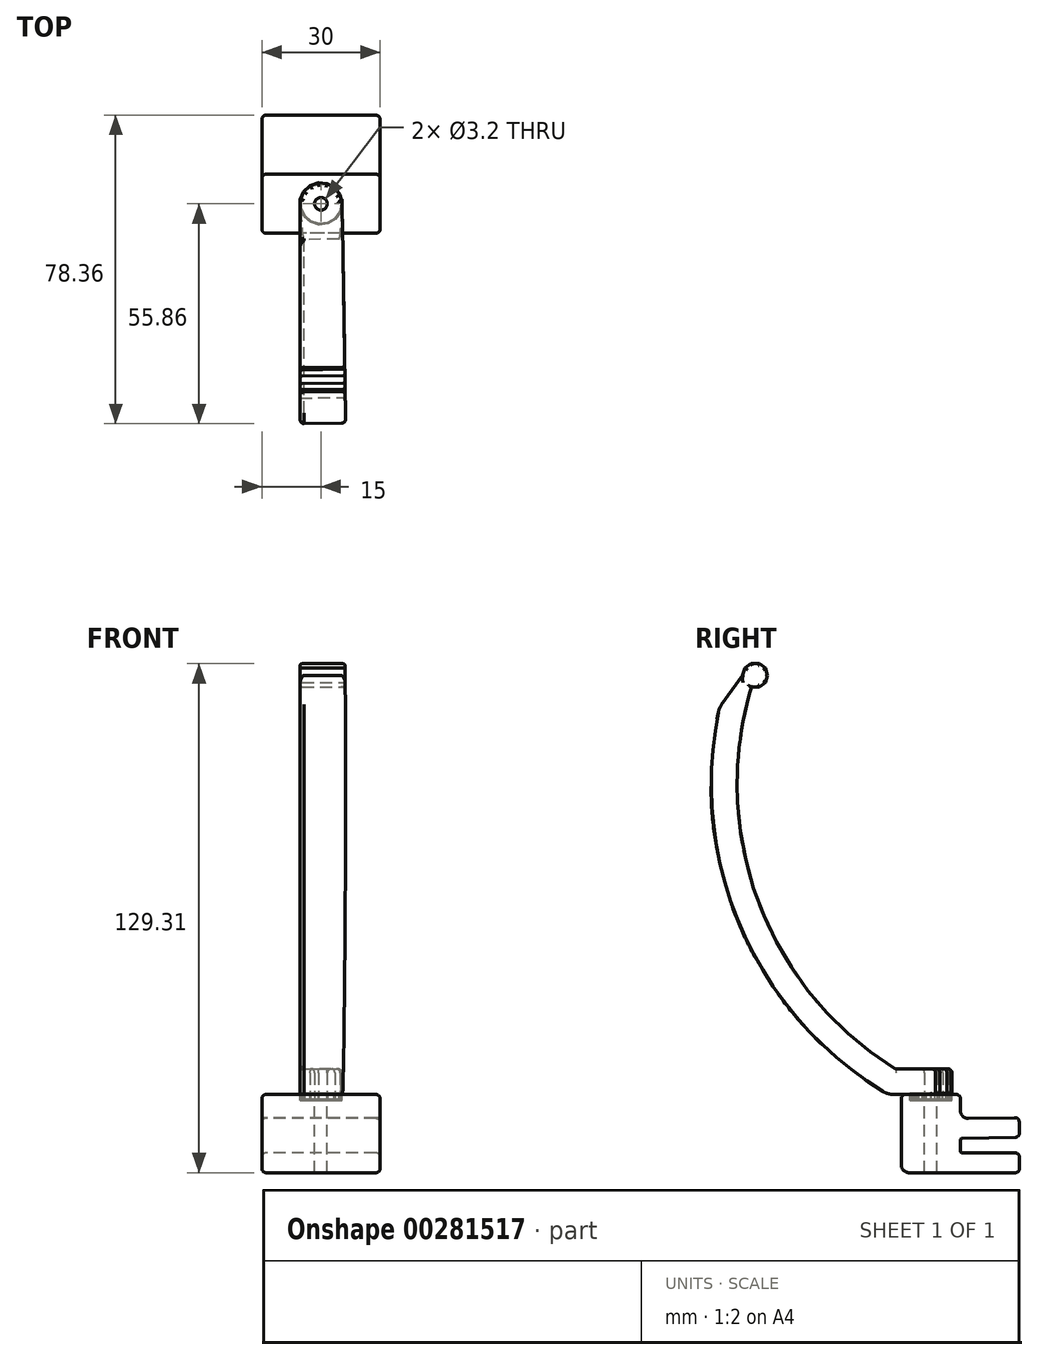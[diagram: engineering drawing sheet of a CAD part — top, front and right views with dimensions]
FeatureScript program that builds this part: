
annotation { "Feature Type Name" : "Feature", "Feature Type Description" : "" }
export const myFeature = defineFeature(function(context is Context, id is Id, definition is map)
    precondition{}
    {
        {
            var Q0;
            Q0=qCreatedBy(makeId("Right.planeOp"),FACE);
            var sketch = newSketch(context, id + "F0", { "sketchPlane" : qUnion([Q0])});
            skLineSegment(sketch, "E0", {"start": v(-1, 0) * mm, "end": v(-15, 0) * mm});
            skLineSegment(sketch, "E1", {"start": v(-14.5, 5) * mm, "end": v(-1, 5) * mm});
            skLineSegment(sketch, "E2", {"start": v(0, 4) * mm, "end": v(0, 1) * mm});
            skLineSegment(sketch, "E3", {"start": v(-15, 5.5) * mm, "end": v(-15, 8.26) * mm});
            skLineSegment(sketch, "E4", {"start": v(-1, 8.98) * mm, "end": v(-14.5, 8.76) * mm});
            skLineSegment(sketch, "E5", {"start": v(-0.02, 10) * mm, "end": v(-0.07, 13) * mm});
            skLineSegment(sketch, "E6", {"start": v(-1.08, 13.98) * mm, "end": v(-12.97, 13.78) * mm});
            skLineSegment(sketch, "E7", {"start": v(-15, 0) * mm, "end": v(-28, 0) * mm});
            skLineSegment(sketch, "E8", {"start": v(-30, 2) * mm, "end": v(-30, 12.86) * mm});
            skLineSegment(sketch, "E9", {"start": v(-15, 15.78) * mm, "end": v(-15, 18.86) * mm});
            skPoint(sketch, "E10.visualSharp", {"position": v(-15, 8.75) * mm});
            skArc(sketch, "E10.filletArc", {"start": v(-14.5, 8.76) * mm, "mid": v(-14.86, 8.6) * mm, "end": v(-15, 8.26) * mm});
            skPoint(sketch, "E11.visualSharp", {"position": v(-15, 5) * mm});
            skArc(sketch, "E11.filletArc", {"start": v(-15, 5.5) * mm, "mid": v(-14.85, 5.15) * mm, "end": v(-14.5, 5) * mm});
            skPoint(sketch, "E12.visualSharp", {"position": v(0, 5) * mm});
            skArc(sketch, "E12.filletArc", {"start": v(0, 4) * mm, "mid": v(-0.3, 4.7) * mm, "end": v(-1, 5) * mm});
            skPoint(sketch, "E13.visualSharp", {"position": v(0, 9) * mm});
            skArc(sketch, "E13.filletArc", {"start": v(-1, 8.98) * mm, "mid": v(-0.3, 9.29) * mm, "end": v(-0.02, 10) * mm});
            skPoint(sketch, "E14.visualSharp", {"position": v(-0.08, 14) * mm});
            skArc(sketch, "E14.filletArc", {"start": v(-0.07, 13) * mm, "mid": v(-0.37, 13.7) * mm, "end": v(-1.08, 13.98) * mm});
            skPoint(sketch, "E15.visualSharp", {"position": v(0, 0) * mm});
            skArc(sketch, "E15.filletArc", {"start": v(-1, 0) * mm, "mid": v(-0.3, 0.3) * mm, "end": v(0, 1) * mm});
            skPoint(sketch, "E16.visualSharp", {"position": v(-30, 0) * mm});
            skArc(sketch, "E16.filletArc", {"start": v(-30, 2) * mm, "mid": v(-29.41, 0.59) * mm, "end": v(-28, 0) * mm});
            skPoint(sketch, "E17.visualSharp", {"position": v(-15, 13.75) * mm});
            skArc(sketch, "E17.filletArc", {"start": v(-15, 15.78) * mm, "mid": v(-14.4, 14.36) * mm, "end": v(-12.97, 13.78) * mm});
            skLineSegment(sketch, "E18", {"start": v(-30, 12.86) * mm, "end": v(-30, 18.86) * mm});
            skLineSegment(sketch, "E19", {"start": v(-29, 19.86) * mm, "end": v(-16, 19.86) * mm});
            skPoint(sketch, "E20.orphan", {"position": v(-15, 12.86) * mm});
            skPoint(sketch, "E21.visualSharp", {"position": v(-15, 19.86) * mm});
            skArc(sketch, "E21.filletArc", {"start": v(-15, 18.86) * mm, "mid": v(-15.3, 19.57) * mm, "end": v(-16, 19.86) * mm});
            skPoint(sketch, "E22.visualSharp", {"position": v(-30, 19.86) * mm});
            skArc(sketch, "E22.filletArc", {"start": v(-29, 19.86) * mm, "mid": v(-29.7, 19.57) * mm, "end": v(-30, 18.86) * mm});
            skSolve(sketch);
        }
        {
            var Q0;
            Q0=makeQuery(id+"F0.imprint","IMPRINT",FACE,{"disambiguationData":[TD([[makeQuery(id+"F0.imprint","IMPRINT",EDGE,{"derivedFrom":sQuery(id+"F0.wireOp",EDGE,"E0")}),-1.0]])]});
            extrude(context, id + "F1", {"entities" : qUnion([Q0]), "endBound" : BoundingType.SYMMETRIC, "depth" : 30 * mm});
        }
        {
            var Q0;
            Q0=makeQuery(id+"F1.opExtrude","CAP_FACE",FACE,{"disambiguationData":[OSD([sQuery(id+"F0.wireOp",EDGE,"E0"),sQuery(id+"F0.wireOp",EDGE,"E1"),sQuery(id+"F0.wireOp",EDGE,"E2"),sQuery(id+"F0.wireOp",EDGE,"E3"),sQuery(id+"F0.wireOp",EDGE,"E4"),sQuery(id+"F0.wireOp",EDGE,"E5"),sQuery(id+"F0.wireOp",EDGE,"E6"),sQuery(id+"F0.wireOp",EDGE,"E7"),sQuery(id+"F0.wireOp",EDGE,"E8"),sQuery(id+"F0.wireOp",EDGE,"E9"),sQuery(id+"F0.wireOp",EDGE,"E10.filletArc"),sQuery(id+"F0.wireOp",EDGE,"E11.filletArc"),sQuery(id+"F0.wireOp",EDGE,"E12.filletArc"),sQuery(id+"F0.wireOp",EDGE,"E13.filletArc"),sQuery(id+"F0.wireOp",EDGE,"E14.filletArc"),sQuery(id+"F0.wireOp",EDGE,"E15.filletArc"),sQuery(id+"F0.wireOp",EDGE,"E16.filletArc"),sQuery(id+"F0.wireOp",EDGE,"E17.filletArc"),sQuery(id+"F0.wireOp",EDGE,"E18"),sQuery(id+"F0.wireOp",EDGE,"E19"),sQuery(id+"F0.wireOp",EDGE,"E21.filletArc"),sQuery(id+"F0.wireOp",EDGE,"E22.filletArc")])],"isStart":false});
            var Q1;
            Q1=makeQuery(id+"F1.opExtrude","CAP_FACE",FACE,{"disambiguationData":[OSD([sQuery(id+"F0.wireOp",EDGE,"E0"),sQuery(id+"F0.wireOp",EDGE,"E1"),sQuery(id+"F0.wireOp",EDGE,"E2"),sQuery(id+"F0.wireOp",EDGE,"E3"),sQuery(id+"F0.wireOp",EDGE,"E4"),sQuery(id+"F0.wireOp",EDGE,"E5"),sQuery(id+"F0.wireOp",EDGE,"E6"),sQuery(id+"F0.wireOp",EDGE,"E7"),sQuery(id+"F0.wireOp",EDGE,"E8"),sQuery(id+"F0.wireOp",EDGE,"E9"),sQuery(id+"F0.wireOp",EDGE,"E10.filletArc"),sQuery(id+"F0.wireOp",EDGE,"E11.filletArc"),sQuery(id+"F0.wireOp",EDGE,"E12.filletArc"),sQuery(id+"F0.wireOp",EDGE,"E13.filletArc"),sQuery(id+"F0.wireOp",EDGE,"E14.filletArc"),sQuery(id+"F0.wireOp",EDGE,"E15.filletArc"),sQuery(id+"F0.wireOp",EDGE,"E16.filletArc"),sQuery(id+"F0.wireOp",EDGE,"E17.filletArc"),sQuery(id+"F0.wireOp",EDGE,"E18"),sQuery(id+"F0.wireOp",EDGE,"E19"),sQuery(id+"F0.wireOp",EDGE,"E21.filletArc"),sQuery(id+"F0.wireOp",EDGE,"E22.filletArc")])],"isStart":true});
            fillet(context, id + "F2", {"entities" : qUnion([Q0, Q1]), "radius" : 1 * mm, "tangentPropagation" : true, "allowEdgeOverflow" : false});
        }
        {
            var Q0;
            Q0=makeQuery(id+"F1.opExtrude","SWEPT_FACE",FACE,{"disambiguationData":[OSD([sQuery(id+"F0.wireOp",EDGE,"E9")])]});
            var sketch = newSketch(context, id + "F3", { "sketchPlane" : qUnion([Q0])});
            skLineSegment(sketch, "E23", {"start": v(0, 14.11) * mm, "end": v(4, 14.11) * mm});
            skLineSegment(sketch, "E24", {"start": v(4, 14.11) * mm, "end": v(1.9, 20.03) * mm});
            skLineSegment(sketch, "E25", {"start": v(1.9, 20.03) * mm, "end": v(0, 20.03) * mm});
            skLineSegment(sketch, "E26.MirrorCS", {"start": v(-1.9, 20.03) * mm, "end": v(0, 20.03) * mm});
            skLineSegment(sketch, "E27.MirrorCS", {"start": v(-4, 14.11) * mm, "end": v(-1.9, 20.03) * mm});
            skLineSegment(sketch, "E28.MirrorCS", {"start": v(0, 14.11) * mm, "end": v(-4, 14.11) * mm});
            skSolve(sketch);
        }
        {
            var Q0;
            Q0 = qSketchRegion(id + "F3", true);
            extrude(context, id + "F4", {"entities" : qUnion([Q0]), "oppositeDirection" : true, "depth" : 22 * mm});
        }
        {
            var Q0;
            Q0=makeQuery(id+"F4.opExtrude","SWEPT_BODY",BODY,{"disambiguationData":[OSD([sQuery(id+"F3.wireOp",EDGE,"E23"),sQuery(id+"F3.wireOp",EDGE,"E24"),sQuery(id+"F3.wireOp",EDGE,"E25"),sQuery(id+"F3.wireOp",EDGE,"E26.MirrorCS"),sQuery(id+"F3.wireOp",EDGE,"E27.MirrorCS"),sQuery(id+"F3.wireOp",EDGE,"E28.MirrorCS")])]});
            var Q1;
            Q1=makeQuery(id+"F1.opExtrude","SWEPT_BODY",BODY,{"disambiguationData":[OSD([sQuery(id+"F0.wireOp",EDGE,"E0"),sQuery(id+"F0.wireOp",EDGE,"E1"),sQuery(id+"F0.wireOp",EDGE,"E2"),sQuery(id+"F0.wireOp",EDGE,"E3"),sQuery(id+"F0.wireOp",EDGE,"E4"),sQuery(id+"F0.wireOp",EDGE,"E5"),sQuery(id+"F0.wireOp",EDGE,"E6"),sQuery(id+"F0.wireOp",EDGE,"E7"),sQuery(id+"F0.wireOp",EDGE,"E8"),sQuery(id+"F0.wireOp",EDGE,"E9"),sQuery(id+"F0.wireOp",EDGE,"E10.filletArc"),sQuery(id+"F0.wireOp",EDGE,"E11.filletArc"),sQuery(id+"F0.wireOp",EDGE,"E12.filletArc"),sQuery(id+"F0.wireOp",EDGE,"E13.filletArc"),sQuery(id+"F0.wireOp",EDGE,"E14.filletArc"),sQuery(id+"F0.wireOp",EDGE,"E15.filletArc"),sQuery(id+"F0.wireOp",EDGE,"E16.filletArc"),sQuery(id+"F0.wireOp",EDGE,"E17.filletArc"),sQuery(id+"F0.wireOp",EDGE,"E18"),sQuery(id+"F0.wireOp",EDGE,"E19"),sQuery(id+"F0.wireOp",EDGE,"E21.filletArc"),sQuery(id+"F0.wireOp",EDGE,"E22.filletArc")])]});
            var Q2;
            Q2=makeQuery(id+"F4.opExtrude","SWEPT_BODY",BODY,{"disambiguationData":[OSD([sQuery(id+"F3.wireOp",EDGE,"E23"),sQuery(id+"F3.wireOp",EDGE,"E24"),sQuery(id+"F3.wireOp",EDGE,"E25"),sQuery(id+"F3.wireOp",EDGE,"E26.MirrorCS"),sQuery(id+"F3.wireOp",EDGE,"E27.MirrorCS"),sQuery(id+"F3.wireOp",EDGE,"E28.MirrorCS")])]});
            var Q3;
            Q3=makeQuery(id+"F4.opExtrude","SWEPT_FACE",FACE,{"disambiguationData":[OSD([sQuery(id+"F3.wireOp",EDGE,"E27.MirrorCS")])]});
            var Q4;
            Q4=makeQuery(id+"F4.opExtrude","SWEPT_FACE",FACE,{"disambiguationData":[OSD([sQuery(id+"F3.wireOp",EDGE,"E24")])]});
            booleanBodies(context, id + "F5", {"operationType" : BooleanOperationType.SUBTRACTION, "tools" : qUnion([Q0, Q1]), "targets" : qUnion([Q2]), "offset" : true, "entitiesToOffset" : qUnion([Q3, Q4]), "offsetDistance" : 0.5 * mm, "keepTools" : true});
        }
        {
            var Q0;
            Q0=makeQuery(id+"F1.opExtrude","SWEPT_FACE",FACE,{"disambiguationData":[OSD([sQuery(id+"F0.wireOp",EDGE,"E19")])]});
            var sketch = newSketch(context, id + "F6", { "sketchPlane" : qUnion([Q0])});
            skCircle(sketch, "E29", {"center": v(0, -22.5) * mm, "radius": 1.6 * mm});
            skPoint(sketch, "E29.centerSnap0", {"position": v(14, -22.5) * mm});
            skPoint(sketch, "E29.centerSnap1", {"position": v(0, -16) * mm});
            skCircle(sketch, "E30.cCircle", {"center": v(0, -22.5) * mm, "radius": 5.39 * mm, "construction": true});
            skLineSegment(sketch, "E30.0", {"start": v(-0.65, -17.15) * mm, "end": v(1.58, -17.35) * mm});
            skLineSegment(sketch, "E30.1", {"start": v(1.58, -17.35) * mm, "end": v(3.54, -18.44) * mm});
            skLineSegment(sketch, "E30.2", {"start": v(3.54, -18.44) * mm, "end": v(4.89, -20.23) * mm});
            skLineSegment(sketch, "E30.3", {"start": v(4.89, -20.23) * mm, "end": v(5.38, -22.42) * mm});
            skLineSegment(sketch, "E30.4", {"start": v(5.38, -22.42) * mm, "end": v(4.95, -24.61) * mm});
            skLineSegment(sketch, "E30.5", {"start": v(4.95, -24.61) * mm, "end": v(3.66, -26.45) * mm});
            skLineSegment(sketch, "E30.6", {"start": v(3.66, -26.45) * mm, "end": v(1.74, -27.6) * mm});
            skLineSegment(sketch, "E30.7", {"start": v(1.74, -27.6) * mm, "end": v(-0.48, -27.86) * mm});
            skLineSegment(sketch, "E30.8", {"start": v(-0.48, -27.86) * mm, "end": v(-2.62, -27.2) * mm});
            skLineSegment(sketch, "E30.9", {"start": v(-2.62, -27.2) * mm, "end": v(-4.3, -25.73) * mm});
            skLineSegment(sketch, "E30.10", {"start": v(-4.3, -25.73) * mm, "end": v(-5.25, -23.7) * mm});
            skLineSegment(sketch, "E30.11", {"start": v(-5.25, -23.7) * mm, "end": v(-5.28, -21.46) * mm});
            skLineSegment(sketch, "E30.12", {"start": v(-5.28, -21.46) * mm, "end": v(-4.4, -19.4) * mm});
            skLineSegment(sketch, "E30.13", {"start": v(-4.4, -19.4) * mm, "end": v(-2.76, -17.88) * mm});
            skLineSegment(sketch, "E30.14", {"start": v(-2.76, -17.88) * mm, "end": v(-0.65, -17.15) * mm});
            skSolve(sketch);
        }
        {
            var Q0;
            Q0=makeQuery(id+"F6.imprint","IMPRINT",FACE,{"disambiguationData":[TD([[makeQuery(id+"F6.imprint","IMPRINT",EDGE,{"derivedFrom":sQuery(id+"F6.wireOp",EDGE,"E29")}),1.0]])]});
            extrude(context, id + "F7", {"entities" : qUnion([Q0]), "operationType" : NewBodyOperationType.REMOVE, "endBound" : BoundingType.THROUGH_ALL, "oppositeDirection" : true, "depth" : 25 * mm});
        }
        {
            var Q0;
            Q0 = qSketchRegion(id + "F6", true);
            extrude(context, id + "F8", {"entities" : qUnion([Q0]), "operationType" : NewBodyOperationType.REMOVE, "oppositeDirection" : true, "depth" : 1.5 * mm});
        }
        {
            var Q0;
            Q0=makeQuery(id+"F8.boolean.opBoolean","COPY",FACE,{"derivedFrom":makeQuery(id+"F8.opExtrude","CAP_FACE",FACE,{"disambiguationData":[OSD([sQuery(id+"F6.wireOp",EDGE,"E29"),sQuery(id+"F6.wireOp",EDGE,"E30.0"),sQuery(id+"F6.wireOp",EDGE,"E30.1"),sQuery(id+"F6.wireOp",EDGE,"E30.2"),sQuery(id+"F6.wireOp",EDGE,"E30.3"),sQuery(id+"F6.wireOp",EDGE,"E30.4"),sQuery(id+"F6.wireOp",EDGE,"E30.5"),sQuery(id+"F6.wireOp",EDGE,"E30.6"),sQuery(id+"F6.wireOp",EDGE,"E30.7"),sQuery(id+"F6.wireOp",EDGE,"E30.8"),sQuery(id+"F6.wireOp",EDGE,"E30.9"),sQuery(id+"F6.wireOp",EDGE,"E30.10"),sQuery(id+"F6.wireOp",EDGE,"E30.11"),sQuery(id+"F6.wireOp",EDGE,"E30.12"),sQuery(id+"F6.wireOp",EDGE,"E30.13"),sQuery(id+"F6.wireOp",EDGE,"E30.14")])],"isStart":false})});
            extrude(context, id + "F9", {"entities" : qUnion([Q0]), "depth" : 3 * mm});
        }
        {
            var Q0;
            Q0=makeQuery(id+"F1.opExtrude","SWEPT_BODY",BODY,{"disambiguationData":[OSD([sQuery(id+"F0.wireOp",EDGE,"E0"),sQuery(id+"F0.wireOp",EDGE,"E1"),sQuery(id+"F0.wireOp",EDGE,"E2"),sQuery(id+"F0.wireOp",EDGE,"E3"),sQuery(id+"F0.wireOp",EDGE,"E4"),sQuery(id+"F0.wireOp",EDGE,"E5"),sQuery(id+"F0.wireOp",EDGE,"E6"),sQuery(id+"F0.wireOp",EDGE,"E7"),sQuery(id+"F0.wireOp",EDGE,"E8"),sQuery(id+"F0.wireOp",EDGE,"E9"),sQuery(id+"F0.wireOp",EDGE,"E10.filletArc"),sQuery(id+"F0.wireOp",EDGE,"E11.filletArc"),sQuery(id+"F0.wireOp",EDGE,"E12.filletArc"),sQuery(id+"F0.wireOp",EDGE,"E13.filletArc"),sQuery(id+"F0.wireOp",EDGE,"E14.filletArc"),sQuery(id+"F0.wireOp",EDGE,"E15.filletArc"),sQuery(id+"F0.wireOp",EDGE,"E16.filletArc"),sQuery(id+"F0.wireOp",EDGE,"E17.filletArc"),sQuery(id+"F0.wireOp",EDGE,"E18"),sQuery(id+"F0.wireOp",EDGE,"E19"),sQuery(id+"F0.wireOp",EDGE,"E21.filletArc"),sQuery(id+"F0.wireOp",EDGE,"E22.filletArc")])]});
            var Q1;
            Q1=makeQuery(id+"F9.opExtrude","SWEPT_BODY",BODY,{"disambiguationData":[OSD([sQuery(id+"F6.wireOp",EDGE,"E29"),sQuery(id+"F6.wireOp",EDGE,"E30.0"),sQuery(id+"F6.wireOp",EDGE,"E30.1"),sQuery(id+"F6.wireOp",EDGE,"E30.2"),sQuery(id+"F6.wireOp",EDGE,"E30.3"),sQuery(id+"F6.wireOp",EDGE,"E30.4"),sQuery(id+"F6.wireOp",EDGE,"E30.5"),sQuery(id+"F6.wireOp",EDGE,"E30.6"),sQuery(id+"F6.wireOp",EDGE,"E30.7"),sQuery(id+"F6.wireOp",EDGE,"E30.8"),sQuery(id+"F6.wireOp",EDGE,"E30.9"),sQuery(id+"F6.wireOp",EDGE,"E30.10"),sQuery(id+"F6.wireOp",EDGE,"E30.11"),sQuery(id+"F6.wireOp",EDGE,"E30.12"),sQuery(id+"F6.wireOp",EDGE,"E30.13"),sQuery(id+"F6.wireOp",EDGE,"E30.14")])]});
            booleanBodies(context, id + "F10", {"operationType" : BooleanOperationType.SUBTRACTION, "tools" : qUnion([Q0]), "targets" : qUnion([Q1]), "offset" : true, "offsetAll" : true, "offsetDistance" : 0.3 * mm, "keepTools" : true});
        }
        {
            var Q0;
            Q0=makeQuery(id+"F9.opExtrude","CAP_FACE",FACE,{"disambiguationData":[OSD([sQuery(id+"F6.wireOp",EDGE,"E29"),sQuery(id+"F6.wireOp",EDGE,"E30.0"),sQuery(id+"F6.wireOp",EDGE,"E30.1"),sQuery(id+"F6.wireOp",EDGE,"E30.2"),sQuery(id+"F6.wireOp",EDGE,"E30.3"),sQuery(id+"F6.wireOp",EDGE,"E30.4"),sQuery(id+"F6.wireOp",EDGE,"E30.5"),sQuery(id+"F6.wireOp",EDGE,"E30.6"),sQuery(id+"F6.wireOp",EDGE,"E30.7"),sQuery(id+"F6.wireOp",EDGE,"E30.8"),sQuery(id+"F6.wireOp",EDGE,"E30.9"),sQuery(id+"F6.wireOp",EDGE,"E30.10"),sQuery(id+"F6.wireOp",EDGE,"E30.11"),sQuery(id+"F6.wireOp",EDGE,"E30.12"),sQuery(id+"F6.wireOp",EDGE,"E30.13"),sQuery(id+"F6.wireOp",EDGE,"E30.14")])],"isStart":false});
            var sketch = newSketch(context, id + "F11", { "sketchPlane" : qUnion([Q0])});
            skLineSegment(sketch, "E31", {"start": v(-5.28, -21.46) * mm, "end": v(-5.28, -31.63) * mm});
            skLineSegment(sketch, "E32", {"start": v(-5.28, -21.46) * mm, "end": v(5.38, -21.3) * mm});
            skLineSegment(sketch, "E33", {"start": v(5.38, -21.3) * mm, "end": v(5.54, -31.46) * mm});
            skLineSegment(sketch, "E34", {"start": v(5.54, -31.46) * mm, "end": v(-5.28, -31.63) * mm});
            skSolve(sketch);
        }
        {
            var Q0;
            Q0=makeQuery(id+"F11.imprint","IMPRINT",FACE,{"disambiguationData":[TD([[makeQuery(id+"F11.imprint","IMPRINT",EDGE,{"derivedFrom":sQuery(id+"F11.wireOp",EDGE,"E31")}),1.0]])]});
            extrude(context, id + "F12", {"entities" : qUnion([Q0]), "oppositeDirection" : true, "depth" : 1.5 * mm});
        }
        {
            var Q0;
            Q0=makeQuery(id+"F12.opExtrude","SWEPT_BODY",BODY,{"disambiguationData":[OSD([sQuery(id+"F6.wireOp",EDGE,"E30.3"),sQuery(id+"F6.wireOp",EDGE,"E30.4"),sQuery(id+"F6.wireOp",EDGE,"E30.5"),sQuery(id+"F6.wireOp",EDGE,"E30.6"),sQuery(id+"F6.wireOp",EDGE,"E30.7"),sQuery(id+"F6.wireOp",EDGE,"E30.8"),sQuery(id+"F6.wireOp",EDGE,"E30.9"),sQuery(id+"F6.wireOp",EDGE,"E30.10"),sQuery(id+"F6.wireOp",EDGE,"E30.11"),sQuery(id+"F11.wireOp",EDGE,"E31"),sQuery(id+"F11.wireOp",EDGE,"E32"),sQuery(id+"F11.wireOp",EDGE,"E33"),sQuery(id+"F11.wireOp",EDGE,"GAi3DVxJ-BXwI-Xczv-j371-Lx2mHJkDYnMB")])]});
            var Q1;
            Q1=makeQuery(id+"F9.opExtrude","SWEPT_BODY",BODY,{"disambiguationData":[OSD([sQuery(id+"F6.wireOp",EDGE,"E29"),sQuery(id+"F6.wireOp",EDGE,"E30.0"),sQuery(id+"F6.wireOp",EDGE,"E30.1"),sQuery(id+"F6.wireOp",EDGE,"E30.2"),sQuery(id+"F6.wireOp",EDGE,"E30.3"),sQuery(id+"F6.wireOp",EDGE,"E30.4"),sQuery(id+"F6.wireOp",EDGE,"E30.5"),sQuery(id+"F6.wireOp",EDGE,"E30.6"),sQuery(id+"F6.wireOp",EDGE,"E30.7"),sQuery(id+"F6.wireOp",EDGE,"E30.8"),sQuery(id+"F6.wireOp",EDGE,"E30.9"),sQuery(id+"F6.wireOp",EDGE,"E30.10"),sQuery(id+"F6.wireOp",EDGE,"E30.11"),sQuery(id+"F6.wireOp",EDGE,"E30.12"),sQuery(id+"F6.wireOp",EDGE,"E30.13"),sQuery(id+"F6.wireOp",EDGE,"E30.14")])]});
            booleanBodies(context, id + "F13", {"operationType" : BooleanOperationType.UNION, "tools" : qUnion([Q0, Q1])});
        }
        {
            var Q0;
            {var subQ0=sQuery(id+"F6.wireOp",EDGE,"E30.3");var subQ1=sQuery(id+"F11.wireOp",EDGE,"E32");Q0=makeQuery(id+"F13.opBoolean","SPLIT",EDGE,{"disambiguationData":[topologyDisambiguationEdgeConnected([makeQuery(id+"F9.opExtrude","SWEPT_FACE",FACE,{"disambiguationData":[OSD([subQ0])]})])],"derivedFrom":makeQuery(id+"F12.opExtrude","SWEPT_EDGE",EDGE,{"disambiguationData":[OSD([subQ0,subQ1])]})});}
            fillet(context, id + "F14", {"entities" : qUnion([Q0]), "radius" : 2 * mm, "tangentPropagation" : true, "allowEdgeOverflow" : false});
        }
        {
            var Q0;
            {var subQ0=sQuery(id+"F6.wireOp",EDGE,"E30.11");var subQ1=sQuery(id+"F6.wireOp",EDGE,"E30.10");var subQ2=sQuery(id+"F6.wireOp",EDGE,"E30.9");var subQ3=sQuery(id+"F6.wireOp",EDGE,"E30.8");var subQ4=sQuery(id+"F6.wireOp",EDGE,"E30.7");var subQ5=sQuery(id+"F6.wireOp",EDGE,"E30.6");var subQ6=sQuery(id+"F6.wireOp",EDGE,"E30.5");var subQ7=sQuery(id+"F6.wireOp",EDGE,"E30.4");var subQ8=sQuery(id+"F6.wireOp",EDGE,"E30.3");Q0=makeQuery(id+"F13.opBoolean","MERGE",FACE,{"derivedFrom":[makeQuery(id+"F9.opExtrude","CAP_FACE",FACE,{"disambiguationData":[OSD([sQuery(id+"F6.wireOp",EDGE,"E29"),sQuery(id+"F6.wireOp",EDGE,"E30.0"),sQuery(id+"F6.wireOp",EDGE,"E30.1"),sQuery(id+"F6.wireOp",EDGE,"E30.2"),subQ8,subQ7,subQ6,subQ5,subQ4,subQ3,subQ2,subQ1,subQ0,sQuery(id+"F6.wireOp",EDGE,"E30.12"),sQuery(id+"F6.wireOp",EDGE,"E30.13"),sQuery(id+"F6.wireOp",EDGE,"E30.14")])],"isStart":false}),makeQuery(id+"F12.opExtrude","CAP_FACE",FACE,{"disambiguationData":[OSD([subQ8,subQ7,subQ6,subQ5,subQ4,subQ3,subQ2,subQ1,subQ0,sQuery(id+"F11.wireOp",EDGE,"E31"),sQuery(id+"F11.wireOp",EDGE,"E32"),sQuery(id+"F11.wireOp",EDGE,"E33"),sQuery(id+"F11.wireOp",EDGE,"GAi3DVxJ-BXwI-Xczv-j371-Lx2mHJkDYnMB")])],"isStart":true})]});}
            extrude(context, id + "F15", {"entities" : qUnion([Q0]), "operationType" : NewBodyOperationType.ADD, "depth" : 5 * mm});
        }
        {
            var Q0;
            {var subQ0=sQuery(id+"F11.wireOp",EDGE,"E33");Q0=makeQuery(id+"F15.boolean.opBoolean","MERGE",FACE,{"derivedFrom":[makeQuery(id+"F12.opExtrude","SWEPT_FACE",FACE,{"disambiguationData":[OSD([subQ0])]}),makeQuery(id+"F15.opExtrude","SWEPT_FACE",FACE,{"disambiguationData":[OSD([subQ0])]})]});}
            var sketch = newSketch(context, id + "F16", { "sketchPlane" : qUnion([Q0])});
            skLineSegment(sketch, "E35", {"start": v(-31.54, 26.36) * mm, "end": v(-31.54, 126.36) * mm});
            skLineSegment(sketch, "E36", {"start": v(-67.14, 126.36) * mm, "end": v(-70.24, 126.36) * mm});
            skArc(sketch, "E37", {"start": v(-67.14, 126.36) * mm, "mid": v(-66.87, 70.12) * mm, "end": v(-31.54, 26.36) * mm});
            skArc(sketch, "E38.0", {"start": v(-76.43, 116.98) * mm, "mid": v(-70.73, 62.22) * mm, "end": v(-34.64, 20.64) * mm});
            skCircle(sketch, "E39.cCircle", {"center": v(-67.14, 126.36) * mm, "radius": 3.1 * mm, "construction": true});
            skLineSegment(sketch, "E39.2", {"start": v(-70.24, 126.36) * mm, "end": v(-69.64, 128.18) * mm});
            skLineSegment(sketch, "E39.3", {"start": v(-69.64, 128.18) * mm, "end": v(-68.1, 129.31) * mm});
            skLineSegment(sketch, "E39.4", {"start": v(-68.1, 129.31) * mm, "end": v(-66.18, 129.31) * mm});
            skLineSegment(sketch, "E39.5", {"start": v(-66.18, 129.31) * mm, "end": v(-64.63, 128.18) * mm});
            skLineSegment(sketch, "E39.6", {"start": v(-64.63, 128.18) * mm, "end": v(-64.04, 126.36) * mm});
            skLineSegment(sketch, "E39.7", {"start": v(-64.04, 126.36) * mm, "end": v(-64.63, 124.54) * mm});
            skLineSegment(sketch, "E39.8", {"start": v(-64.63, 124.54) * mm, "end": v(-66.18, 123.41) * mm});
            skLineSegment(sketch, "E39.9", {"start": v(-66.18, 123.41) * mm, "end": v(-68.1, 123.41) * mm});
            skPoint(sketch, "E40.orphan", {"position": v(-70.24, 126.36) * mm});
            skLineSegment(sketch, "E41", {"start": v(-70.24, 126.36) * mm, "end": v(-75.6, 118.89) * mm});
            skPoint(sketch, "E42.visualSharp", {"position": v(-76.2, 118.03) * mm});
            skArc(sketch, "E42.filletArc", {"start": v(-75.6, 118.89) * mm, "mid": v(-76.11, 117.98) * mm, "end": v(-76.43, 116.98) * mm});
            skLineSegment(sketch, "E43", {"start": v(-31.54, 19.86) * mm, "end": v(-32.32, 19.9) * mm});
            skPoint(sketch, "E44.visualSharp", {"position": v(-33.55, 19.98) * mm});
            skArc(sketch, "E44.filletArc", {"start": v(-34.64, 20.64) * mm, "mid": v(-33.53, 20.13) * mm, "end": v(-32.32, 19.9) * mm});
            skSolve(sketch);
        }
        {
            var Q0;
            Q0=makeQuery(id+"F16.imprint","IMPRINT",FACE,{"disambiguationData":[TD([[makeQuery(id+"F16.imprint","IMPRINT",EDGE,{"derivedFrom":sQuery(id+"F16.wireOp",EDGE,"E37")}),-1.0]])]});
            var Q1;
            {var subQ0=sQuery(id+"F11.wireOp",EDGE,"E31");Q1=makeQuery(id+"F15.boolean.opBoolean","MERGE",FACE,{"derivedFrom":[makeQuery(id+"F12.opExtrude","SWEPT_FACE",FACE,{"disambiguationData":[OSD([subQ0])]}),makeQuery(id+"F15.opExtrude","SWEPT_FACE",FACE,{"disambiguationData":[OSD([subQ0])]})]});}
            extrude(context, id + "F17", {"entities" : qUnion([Q0]), "operationType" : NewBodyOperationType.ADD, "endBound" : BoundingType.UP_TO_SURFACE, "oppositeDirection" : true, "endBoundEntityFace" : qUnion([Q1]), "depth" : 25 * mm});
        }
        {
            var Q0;
            {var subQ0=sQuery(id+"F16.wireOp",EDGE,"E39.2");Q0=makeQuery(id+"F16.imprint","IMPRINT",FACE,{"disambiguationData":[TD([[makeQuery(id+"F16.imprint","IMPRINT",EDGE,{"derivedFrom":subQ0}),-1.0]])]});}
            var Q1;
            {var subQ0=sQuery(id+"F11.wireOp",EDGE,"E31");Q1=makeQuery(id+"F17.boolean.opBoolean","MERGE",FACE,{"derivedFrom":[makeQuery(id+"F15.boolean.opBoolean","MERGE",FACE,{"derivedFrom":[makeQuery(id+"F12.opExtrude","SWEPT_FACE",FACE,{"disambiguationData":[OSD([subQ0])]}),makeQuery(id+"F15.opExtrude","SWEPT_FACE",FACE,{"disambiguationData":[OSD([subQ0])]})]}),makeQuery(id+"F17.opExtrude","CAP_FACE",FACE,{"disambiguationData":[OSD([sQuery(id+"F11.wireOp",EDGE,"E33"),sQuery(id+"F11.wireOp",EDGE,"E34"),sQuery(id+"F16.wireOp",EDGE,"E36"),sQuery(id+"F16.wireOp",EDGE,"E37"),sQuery(id+"F16.wireOp",EDGE,"E38.0"),sQuery(id+"F16.wireOp",EDGE,"E41"),sQuery(id+"F16.wireOp",EDGE,"E42.filletArc"),sQuery(id+"F16.wireOp",EDGE,"E43"),sQuery(id+"F16.wireOp",EDGE,"E44.filletArc")])],"isStart":false})]});}
            extrude(context, id + "F18", {"entities" : qUnion([Q0]), "operationType" : NewBodyOperationType.ADD, "endBound" : BoundingType.UP_TO_SURFACE, "oppositeDirection" : true, "endBoundEntityFace" : qUnion([Q1]), "depth" : 8.4 * mm});
        }
        {
            var Q0;
            Q0=makeQuery(id+"F17.opExtrude","CAP_EDGE",EDGE,{"disambiguationData":[OSD([sQuery(id+"F16.wireOp",EDGE,"E37")])],"isStart":true});
            var Q1;
            Q1=makeQuery(id+"F17.opExtrude","CAP_EDGE",EDGE,{"disambiguationData":[OSD([sQuery(id+"F16.wireOp",EDGE,"E38.0")])],"isStart":true});
            var Q2;
            Q2=makeQuery(id+"F15.opExtrude","CAP_EDGE",EDGE,{"disambiguationData":[OSD([sQuery(id+"F11.wireOp",EDGE,"E33")])],"isStart":false});
            var Q3;
            Q3=makeQuery(id+"F15.opExtrude","CAP_FACE",FACE,{"disambiguationData":[OSD([sQuery(id+"F6.wireOp",EDGE,"E29"),sQuery(id+"F6.wireOp",EDGE,"E30.0"),sQuery(id+"F6.wireOp",EDGE,"E30.1"),sQuery(id+"F6.wireOp",EDGE,"E30.2"),sQuery(id+"F6.wireOp",EDGE,"E30.3"),sQuery(id+"F6.wireOp",EDGE,"E30.4"),sQuery(id+"F6.wireOp",EDGE,"E30.5"),sQuery(id+"F6.wireOp",EDGE,"E30.6"),sQuery(id+"F6.wireOp",EDGE,"E30.7"),sQuery(id+"F6.wireOp",EDGE,"E30.8"),sQuery(id+"F6.wireOp",EDGE,"E30.9"),sQuery(id+"F6.wireOp",EDGE,"E30.10"),sQuery(id+"F6.wireOp",EDGE,"E30.11"),sQuery(id+"F6.wireOp",EDGE,"E30.12"),sQuery(id+"F6.wireOp",EDGE,"E30.13"),sQuery(id+"F6.wireOp",EDGE,"E30.14"),sQuery(id+"F11.wireOp",EDGE,"E31"),sQuery(id+"F11.wireOp",EDGE,"E32"),sQuery(id+"F11.wireOp",EDGE,"E33"),sQuery(id+"F11.wireOp",EDGE,"E34")])],"isStart":false});
            var Q4;
            Q4=makeQuery(id+"F17.opExtrude","CAP_EDGE",EDGE,{"disambiguationData":[OSD([sQuery(id+"F16.wireOp",EDGE,"E38.0")])],"isStart":false});
            fillet(context, id + "F19", {"entities" : qUnion([Q0, Q1, Q2, Q3, Q4]), "radius" : 1 * mm, "tangentPropagation" : true, "allowEdgeOverflow" : false});
        }
        {
            var Q0;
            Q0=makeQuery(id+"F18.opExtrude","CAP_EDGE",EDGE,{"disambiguationData":[OSD([sQuery(id+"F16.wireOp",EDGE,"E39.2")])],"isStart":false});
            var Q1;
            Q1=makeQuery(id+"F18.opExtrude","CAP_EDGE",EDGE,{"disambiguationData":[OSD([sQuery(id+"F16.wireOp",EDGE,"E39.3")])],"isStart":false});
            var Q2;
            Q2=makeQuery(id+"F18.opExtrude","CAP_EDGE",EDGE,{"disambiguationData":[OSD([sQuery(id+"F16.wireOp",EDGE,"E39.4")])],"isStart":false});
            var Q3;
            Q3=makeQuery(id+"F18.opExtrude","CAP_EDGE",EDGE,{"disambiguationData":[OSD([sQuery(id+"F16.wireOp",EDGE,"E39.5")])],"isStart":false});
            var Q4;
            Q4=makeQuery(id+"F18.opExtrude","CAP_EDGE",EDGE,{"disambiguationData":[OSD([sQuery(id+"F16.wireOp",EDGE,"E39.6")])],"isStart":false});
            var Q5;
            Q5=makeQuery(id+"F18.opExtrude","CAP_EDGE",EDGE,{"disambiguationData":[OSD([sQuery(id+"F16.wireOp",EDGE,"E39.7")])],"isStart":false});
            var Q6;
            Q6=makeQuery(id+"F18.opExtrude","CAP_EDGE",EDGE,{"disambiguationData":[OSD([sQuery(id+"F16.wireOp",EDGE,"E39.8")])],"isStart":false});
            var Q7;
            Q7=makeQuery(id+"F18.opExtrude","CAP_EDGE",EDGE,{"disambiguationData":[OSD([sQuery(id+"F16.wireOp",EDGE,"E39.9")])],"isStart":false});
            var Q8;
            Q8=makeQuery(id+"F18.opExtrude","CAP_EDGE",EDGE,{"disambiguationData":[OSD([sQuery(id+"F16.wireOp",EDGE,"E39.2")])],"isStart":true});
            var Q9;
            Q9=makeQuery(id+"F18.opExtrude","CAP_EDGE",EDGE,{"disambiguationData":[OSD([sQuery(id+"F16.wireOp",EDGE,"E39.3")])],"isStart":true});
            var Q10;
            Q10=makeQuery(id+"F18.opExtrude","CAP_EDGE",EDGE,{"disambiguationData":[OSD([sQuery(id+"F16.wireOp",EDGE,"E39.4")])],"isStart":true});
            var Q11;
            Q11=makeQuery(id+"F18.opExtrude","CAP_EDGE",EDGE,{"disambiguationData":[OSD([sQuery(id+"F16.wireOp",EDGE,"E39.5")])],"isStart":true});
            var Q12;
            Q12=makeQuery(id+"F18.opExtrude","CAP_EDGE",EDGE,{"disambiguationData":[OSD([sQuery(id+"F16.wireOp",EDGE,"E39.6")])],"isStart":true});
            var Q13;
            Q13=makeQuery(id+"F18.opExtrude","CAP_EDGE",EDGE,{"disambiguationData":[OSD([sQuery(id+"F16.wireOp",EDGE,"E39.7")])],"isStart":true});
            var Q14;
            Q14=makeQuery(id+"F18.opExtrude","CAP_EDGE",EDGE,{"disambiguationData":[OSD([sQuery(id+"F16.wireOp",EDGE,"E39.8")])],"isStart":true});
            var Q15;
            Q15=makeQuery(id+"F18.opExtrude","CAP_EDGE",EDGE,{"disambiguationData":[OSD([sQuery(id+"F16.wireOp",EDGE,"E39.9")])],"isStart":true});
            fillet(context, id + "F20", {"entities" : qUnion([Q0, Q1, Q2, Q3, Q4, Q5, Q6, Q7, Q8, Q9, Q10, Q11, Q12, Q13, Q14, Q15]), "radius" : 0.5 * mm, "tangentPropagation" : true, "allowEdgeOverflow" : false});
        }
    });
